# Revit family: MDV-V100W$DHN1(C)
name_source: partatom
category: Mechanical Equipment
revit_build: Autodesk Revit 2013 (Build: 20120221_2030(x64)
units: mm (PartAtom-declared; Revit-internal decimal feet)

## types (1)
- MDV-V100W/DHN1(C)
    Air Flow = 5200.00 m³/h
    Casing color = SB2098
    Compressor = 1
    Condensation = Air
    Cooling Capacity = 10.00 kW
    Cooling Power Input = 2.55 kW
    Depth = 360 mm  [stored 1.1811 ft]
    Description = High efficiency air cooled
    Gas = R410A
    Gas pipe = 15.9 mm
    Gas pipe Radius = 7.95 mm  [stored 0.0260827 ft]
    Heating Capacity = 12.00 kW
    Heating Power Input = 2.87 kW
    Height = 840 mm  [stored 2.75591 ft]
    Installation = Outdoor installation
    Liquid pipe = 9.53 mm
    Liquid pipe Radius = 4.765 mm
    Manufacturer = Midea
    Maximum Fuse Amps = 32 A
    Min cable selection (power wiring) = 3×4 mm2
    Minimum Circuit Amps = 29 A
    Model = MDV-V100W/DHN1(C)
    Net Weight = 71.50 kg
    Power supply = 220-240V 1Ph~50Hz/60Hz
    Series = VRF
    Width = 950 mm
    clearance access behind = 300 mm
    clearance access front = 2000 mm  [stored 6.56168 ft]
    clearance access left = 300 mm
    clearance access right = 600 mm  [stored 1.9685 ft]

note: [stored X ft] marks values corroborated as IEEE doubles in the binary element streams (Revit-internal decimal feet)

## geometry (parser evidence)
native form markers: Sweep x17
no freeform markers — native parametric forms only
